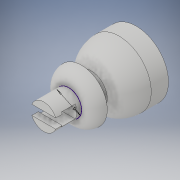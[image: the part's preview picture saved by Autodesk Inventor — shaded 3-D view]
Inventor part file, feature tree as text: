
AUTODESK INVENTOR PART (.ipt)
format: ipt  version: 2018 (Build 220112000, 112)  size: 192,000 bytes
history: native  units: mm
features: sketch x11, extrude x10, fillet x2
ambient origin geometry x8: Origin, YZ Plane, XZ Plane, XY Plane, X Axis, Y Axis, Z Axis, Center Point
bodies: Volumenkörper1 (feature_tree)
feature tree (23):
  extrude  "Extrusion1"  Depth=2.0mm TaperAngle=0.0deg
  fillet  "Rundung1"  Radius=2.0mm
  extrude  "Extrusion2"  Depth=5.0mm TaperAngle=0.0deg
  extrude  "Extrusion3"  Depth=5.0mm TaperAngle=0.0deg
  extrude  "Extrusion5"  Depth=2.0mm TaperAngle=0.0deg
  extrude  "Extrusion6"  Depth=2.0mm TaperAngle=0.0deg
  extrude  "Extrusion7"  Depth=1.1mm TaperAngle=0.0deg
  fillet  "Rundung2"  Radius=5.0mm
  sketch  "Skizze11"  dims[d23=4.0mm d24=4.0mm]
  extrude  "Extrusion8"  Depth=4.0mm
  extrude  "Extrusion9"  Depth=2.15mm TaperAngle=0.0deg
  extrude  "Extrusion10"  Depth=1.0mm TaperAngle=0.0deg
  extrude  "Extrusion11"  [1 undecoded]
  sketch  "Skizze1"  dims[d0=8.0mm d1=2.0mm d2=0.0mm d3=2.0mm]
  sketch  "Skizze2"  dims[d4=5.0mm d5=1.5mm d6=0.0mm]
  sketch  "Skizze3"  dims[d7=10.0mm d8=5.0mm d9=0.0mm]
  sketch  "Skizze5"  dims[d13=10.0mm d14=2.0mm d15=0.0mm]
  sketch  "Skizze6"  dims[d16=8.5mm d17=2.0mm d18=0.0mm]
  sketch  "Skizze8"  dims[d19=1.6mm d20=1.1mm d21=0.0mm d22=5.0mm]
  sketch  "Skizze12"  dims[d25=2.85mm d26=0.0mm d27=2.15mm d28=0.0mm]
  sketch  "Skizze13"  dims[d29=4.0mm d30=1.0mm d31=0.0mm]
  sketch  "Skizze14"  dims[d32=1.0mm d33=0.0mm]
  sketch  "Skizze15"
note: 1 required parameter value undecoded (feature->parameter linkage not recoverable at this tier; creation-order binding heuristic only, values carry confidence <= 0.55)
